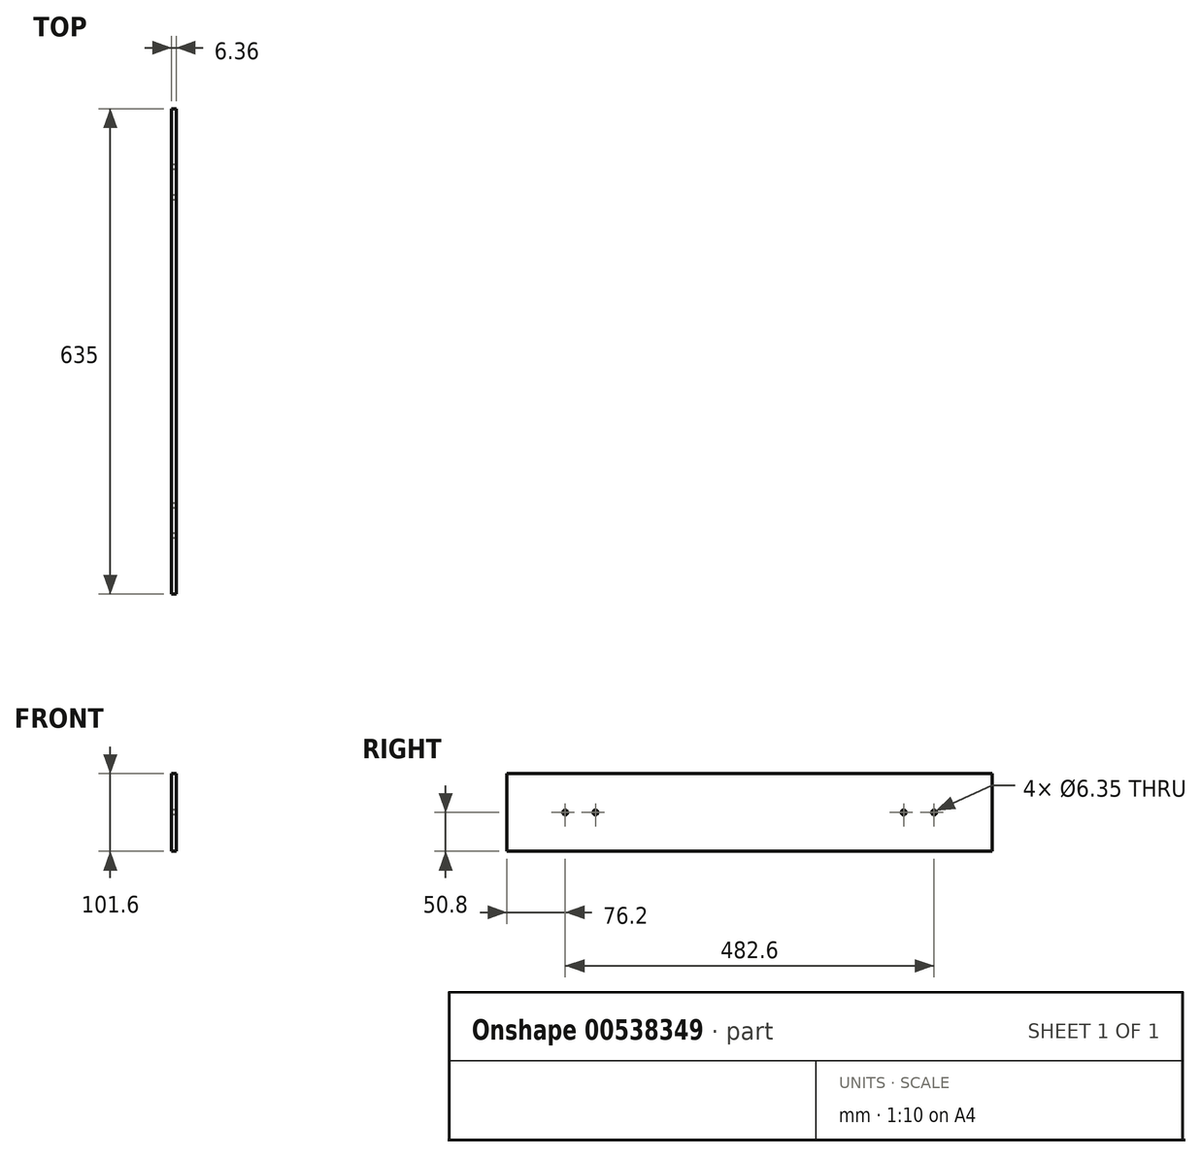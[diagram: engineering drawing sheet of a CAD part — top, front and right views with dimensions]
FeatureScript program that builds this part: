
annotation { "Feature Type Name" : "Feature", "Feature Type Description" : "" }
export const myFeature = defineFeature(function(context is Context, id is Id, definition is map)
    precondition{}
    {
        {
            var Q0;
            Q0=qCreatedBy(makeId("Right.planeOp"),FACE);
            var sketch = newSketch(context, id + "F0", { "sketchPlane" : qUnion([Q0])});
            skLineSegment(sketch, "E0.bottom", {"start": v(317.5, 50.8) * mm, "end": v(-317.5, 50.8) * mm});
            skLineSegment(sketch, "E0.top", {"start": v(317.5, -50.8) * mm, "end": v(-317.5, -50.8) * mm});
            skLineSegment(sketch, "E0.left", {"start": v(317.5, 50.8) * mm, "end": v(317.5, -50.8) * mm});
            skLineSegment(sketch, "E0.right", {"start": v(-317.5, 50.8) * mm, "end": v(-317.5, -50.8) * mm});
            skPoint(sketch, "E0.middle", {"position": v(0, 0) * mm});
            skCircle(sketch, "E1", {"center": v(241.3, 0) * mm, "radius": 3.18 * mm});
            skCircle(sketch, "E2", {"center": v(201.61, 0) * mm, "radius": 3.18 * mm});
            skCircle(sketch, "E3", {"center": v(-241.3, 0) * mm, "radius": 3.18 * mm});
            skLineSegment(sketch, "E4", {"start": v(241.3, 0) * mm, "end": v(317.5, 0) * mm});
            skLineSegment(sketch, "E5", {"start": v(241.3, 0) * mm, "end": v(201.61, 0) * mm});
            skLineSegment(sketch, "E6", {"start": v(201.61, 0) * mm, "end": v(0, 0) * mm});
            skLineSegment(sketch, "E7", {"start": v(-241.3, 0) * mm, "end": v(-317.5, 0) * mm});
            skCircle(sketch, "E8", {"center": v(-201.63, 0) * mm, "radius": 3.18 * mm});
            skLineSegment(sketch, "E9", {"start": v(-201.63, 0) * mm, "end": v(-241.3, 0) * mm});
            skLineSegment(sketch, "E10", {"start": v(0, 0) * mm, "end": v(-201.63, 0) * mm});
            skSolve(sketch);
        }
        {
            var Q0;
            Q0 = qSketchRegion(id + "F0", true);
            extrude(context, id + "F1", {"entities" : qUnion([Q0]), "endBound" : BoundingType.SYMMETRIC, "depth" : 6.35 * mm, "offsetDistance" : 25.4 * mm});
        }
    });
